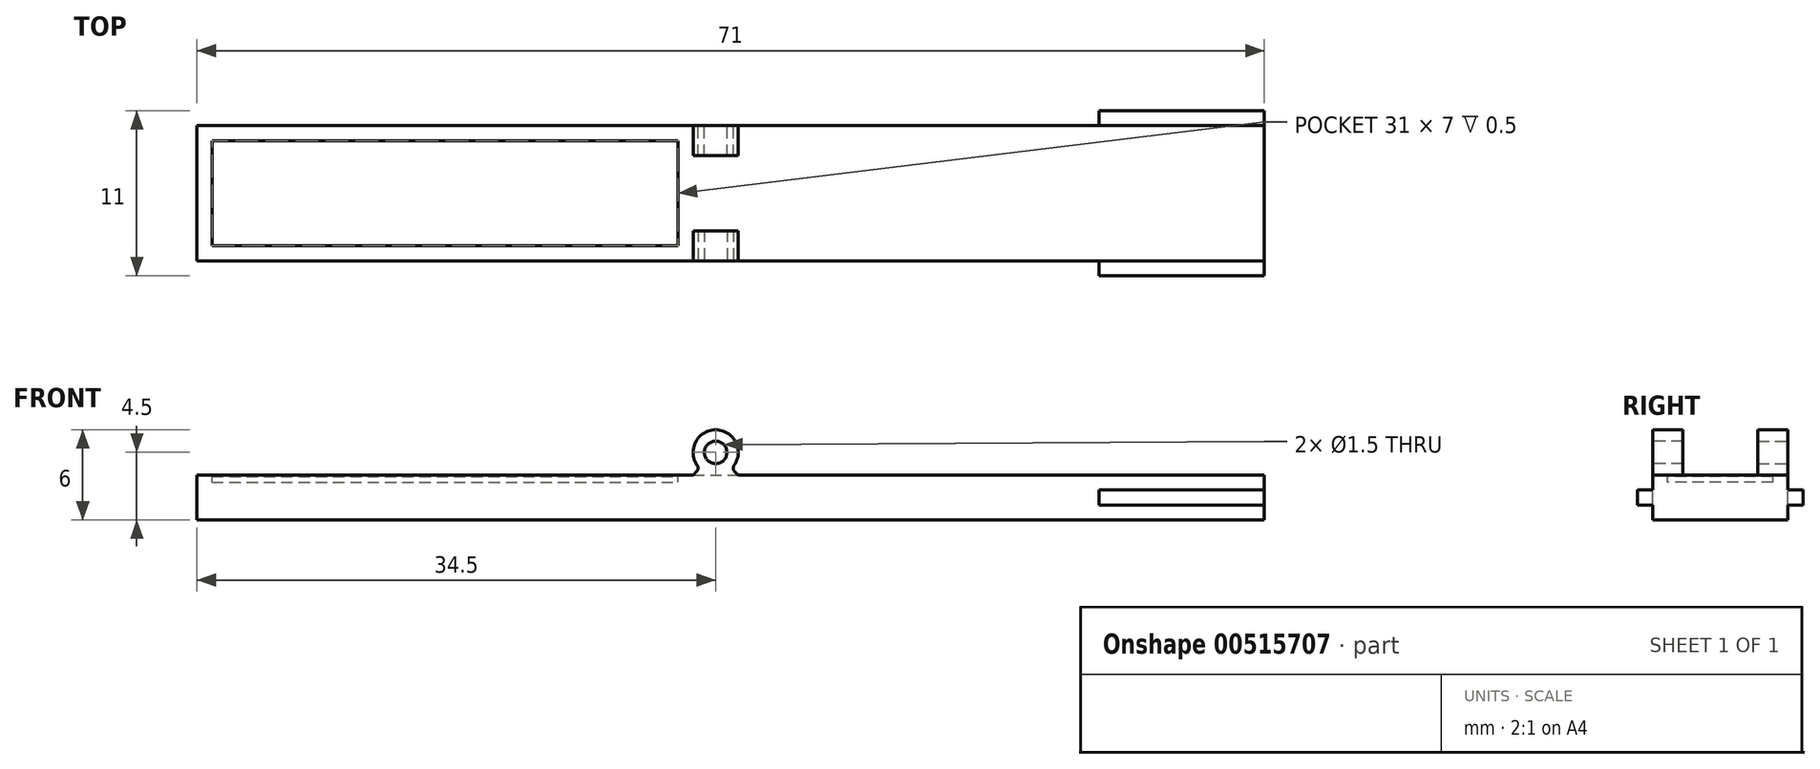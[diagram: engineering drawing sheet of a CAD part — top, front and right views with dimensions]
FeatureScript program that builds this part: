
annotation { "Feature Type Name" : "Feature", "Feature Type Description" : "" }
export const myFeature = defineFeature(function(context is Context, id is Id, definition is map)
    precondition{}
    {
        {
            var Q0;
            Q0=qCreatedBy(makeId("Top.planeOp"),FACE);
            var sketch = newSketch(context, id + "F0", { "sketchPlane" : qUnion([Q0])});
            skLineSegment(sketch, "E0.bottom", {"start": v(-34.5, 4.5) * mm, "end": v(36.5, 4.5) * mm});
            skLineSegment(sketch, "E0.top", {"start": v(-34.5, -4.5) * mm, "end": v(36.5, -4.5) * mm});
            skLineSegment(sketch, "E0.left", {"start": v(-34.5, 4.5) * mm, "end": v(-34.5, -4.5) * mm});
            skLineSegment(sketch, "E0.right", {"start": v(36.5, 4.5) * mm, "end": v(36.5, -4.5) * mm});
            skLineSegment(sketch, "E1", {"start": v(-34.5, 0) * mm, "end": v(36.5, 0) * mm, "construction": true});
            skPoint(sketch, "E1.startSnap0", {"position": v(-34.5, 0) * mm});
            skLineSegment(sketch, "E2", {"start": v(0, 4.5) * mm, "end": v(0, -4.5) * mm, "construction": true});
            skLineSegment(sketch, "E3.bottom", {"start": v(-33.5, 3.5) * mm, "end": v(-2.5, 3.5) * mm});
            skLineSegment(sketch, "E3.top", {"start": v(-33.5, -3.5) * mm, "end": v(-2.5, -3.5) * mm});
            skLineSegment(sketch, "E3.left", {"start": v(-33.5, 3.5) * mm, "end": v(-33.5, -3.5) * mm});
            skLineSegment(sketch, "E3.right", {"start": v(-2.5, 3.5) * mm, "end": v(-2.5, -3.5) * mm});
            skSolve(sketch);
        }
        {
            var Q0;
            Q0=makeQuery(id+"F0.imprint","IMPRINT",FACE,{"disambiguationData":[TD([[makeQuery(id+"F0.imprint","IMPRINT",EDGE,{"derivedFrom":sQuery(id+"F0.wireOp",EDGE,"E0.bottom")}),-1.0]])]});
            var Q1;
            Q1=makeQuery(id+"F0.imprint","IMPRINT",FACE,{"disambiguationData":[TD([[makeQuery(id+"F0.imprint","IMPRINT",EDGE,{"derivedFrom":sQuery(id+"F0.wireOp",EDGE,"E3.bottom")}),-1.0]])]});
            extrude(context, id + "F1", {"entities" : qUnion([Q0, Q1]), "oppositeDirection" : true, "depth" : 3 * mm, "offsetDistance" : 25 * mm});
        }
        {
            var Q0;
            Q0=qCreatedBy(makeId("Front.planeOp"),FACE);
            cPlane(context, id + "F2", {"entities" : qUnion([Q0]), "cplaneType" : CPlaneType.OFFSET, "offset" : 4.5 * mm, "width" : 150 * mm, "height" : 150 * mm});
        }
        {
            var Q0;
            Q0=qCreatedBy(id+"F2.planeOp",FACE);
            var sketch = newSketch(context, id + "F3", { "sketchPlane" : qUnion([Q0])});
            skCircle(sketch, "E4", {"center": v(0, 1.5) * mm, "radius": 1.5 * mm});
            skCircle(sketch, "E5", {"center": v(0, 1.5) * mm, "radius": 0.75 * mm});
            skLineSegment(sketch, "E6", {"start": v(0, -1.6) * mm, "end": v(0, 3.6) * mm, "construction": true});
            skLineSegment(sketch, "E7", {"start": v(1.06, 0.44) * mm, "end": v(1.5, 0) * mm});
            skLineSegment(sketch, "E8", {"start": v(0, 1.5) * mm, "end": v(1.06, 0.44) * mm, "construction": true});
            skLineSegment(sketch, "E9.MirrorCS", {"start": v(-1.06, 0.44) * mm, "end": v(-1.5, 0) * mm});
            skLineSegment(sketch, "E10.0", {"start": v(-1.5, 0) * mm, "end": v(1.5, 0) * mm});
            skPoint(sketch, "E11.orphan", {"position": v(-34.5, 0) * mm});
            skPoint(sketch, "E12.orphan", {"position": v(36.5, 0) * mm});
            skLineSegment(sketch, "E13.right", {"start": v(36.5, -1) * mm, "end": v(36.5, -2) * mm});
            skLineSegment(sketch, "E14.bottom", {"start": v(25.5, -1) * mm, "end": v(35.5, -1) * mm});
            skLineSegment(sketch, "E14.top", {"start": v(25.5, -2) * mm, "end": v(35.5, -2) * mm});
            skLineSegment(sketch, "E14.left", {"start": v(25.5, -1) * mm, "end": v(25.5, -2) * mm});
            skLineSegment(sketch, "E15", {"start": v(18.91, -1.5) * mm, "end": v(36.5, -1.5) * mm, "construction": true});
            skPoint(sketch, "E15.startSnap0", {"position": v(25.5, -1.5) * mm});
            skLineSegment(sketch, "E16", {"start": v(35.5, -2) * mm, "end": v(36.5, -2) * mm});
            skLineSegment(sketch, "E17", {"start": v(35.5, -1) * mm, "end": v(36.5, -1) * mm});
            skPoint(sketch, "E13.top.end.orphan", {"position": v(36.5, -3) * mm});
            skLineSegment(sketch, "E18.0", {"start": v(36.5, -3) * mm, "end": v(36.5, 0) * mm});
            skSolve(sketch);
        }
        {
            var Q0;
            Q0=makeQuery(id+"F3.imprint","IMPRINT",FACE,{"disambiguationData":[TD([[makeQuery(id+"F3.imprint","IMPRINT",EDGE,{"derivedFrom":sQuery(id+"F3.wireOp",EDGE,"E4")}),1.0]])]});
            var Q1;
            {var subQ0=sQuery(id+"F3.wireOp",EDGE,"E9.MirrorCS");Q1=makeQuery(id+"F3.imprint","IMPRINT",FACE,{"disambiguationData":[TD([[makeQuery(id+"F3.imprint","IMPRINT",EDGE,{"derivedFrom":subQ0}),1.0]])]});}
            var Q2;
            {var subQ0=sQuery(id+"F3.wireOp",EDGE,"E7");Q2=makeQuery(id+"F3.imprint","IMPRINT",FACE,{"disambiguationData":[TD([[makeQuery(id+"F3.imprint","IMPRINT",EDGE,{"derivedFrom":subQ0}),-1.0]])]});}
            extrude(context, id + "F4", {"entities" : qUnion([Q0, Q1, Q2]), "operationType" : NewBodyOperationType.ADD, "oppositeDirection" : true, "depth" : 2 * mm, "offsetDistance" : 25 * mm});
        }
        {
            var Q0;
            Q0=makeQuery(id+"F4.opExtrude","SWEPT_EDGE",EDGE,{"disambiguationData":[OSD([sQuery(id+"F3.wireOp",EDGE,"E4"),sQuery(id+"F3.wireOp",EDGE,"E7")])]});
            var Q1;
            Q1=makeQuery(id+"F4.opExtrude","SWEPT_EDGE",EDGE,{"disambiguationData":[OSD([sQuery(id+"F3.wireOp",EDGE,"E4"),sQuery(id+"F3.wireOp",EDGE,"E9.MirrorCS")])]});
            var Q2;
            Q2=makeQuery(id+"F4.opExtrude","SWEPT_EDGE",EDGE,{"disambiguationData":[OSD([sQuery(id+"F3.wireOp",EDGE,"E9.MirrorCS"),sQuery(id+"F3.wireOp",EDGE,"E10.0")])]});
            var Q3;
            Q3=makeQuery(id+"F4.opExtrude","SWEPT_EDGE",EDGE,{"disambiguationData":[OSD([sQuery(id+"F3.wireOp",EDGE,"E7"),sQuery(id+"F3.wireOp",EDGE,"E10.0")])]});
            fillet(context, id + "F5", {"entities" : qUnion([Q0, Q1, Q2, Q3]), "radius" : .3 * mm, "tangentPropagation" : true, "allowEdgeOverflow" : false});
        }
        {
            var Q0;
            Q0=makeQuery(id+"F1.opExtrude","SWEPT_BODY",BODY,{"disambiguationData":[OSD([sQuery(id+"F0.wireOp",EDGE,"E0.bottom"),sQuery(id+"F0.wireOp",EDGE,"E0.top"),sQuery(id+"F0.wireOp",EDGE,"E0.left"),sQuery(id+"F0.wireOp",EDGE,"E0.right")])]});
            var Q1;
            Q1=qCreatedBy(makeId("Front.planeOp"),FACE);
            mirror(context, id + "F6", {"operationType" : NewBodyOperationType.ADD, "entities" : qUnion([Q0]), "mirrorPlane" : qUnion([Q1])});
        }
        {
            var Q0;
            Q0=makeQuery(id+"F3.imprint","IMPRINT",FACE,{"disambiguationData":[TD([[makeQuery(id+"F3.imprint","IMPRINT",EDGE,{"derivedFrom":sQuery(id+"F3.wireOp",EDGE,"E14.bottom")}),-1.0]])]});
            extrude(context, id + "F7", {"entities" : qUnion([Q0]), "operationType" : NewBodyOperationType.ADD, "depth" : 1 * mm, "offsetDistance" : 25 * mm, "hasSecondDirection" : true, "secondDirectionOppositeDirection" : true, "secondDirectionDepth" : 10 * mm});
        }
        {
            var Q0;
            Q0=makeQuery(id+"F0.imprint","IMPRINT",FACE,{"disambiguationData":[TD([[makeQuery(id+"F0.imprint","IMPRINT",EDGE,{"derivedFrom":sQuery(id+"F0.wireOp",EDGE,"E3.bottom")}),-1.0]])]});
            extrude(context, id + "F8", {"entities" : qUnion([Q0]), "operationType" : NewBodyOperationType.REMOVE, "oppositeDirection" : true, "depth" : .5 * mm, "offsetDistance" : 25 * mm});
        }
        {
            var Q0;
            Q0=makeQuery(id+"F0.imprint","IMPRINT",FACE,{"disambiguationData":[TD([[makeQuery(id+"F0.imprint","IMPRINT",EDGE,{"derivedFrom":sQuery(id+"F0.wireOp",EDGE,"E3.bottom")}),-1.0]])]});
            extrude(context, id + "F9", {"entities" : qUnion([Q0]), "oppositeDirection" : true, "depth" : .5 * mm, "offsetDistance" : 25 * mm});
        }
        {
            var Q0;
            Q0=makeQuery(id+"F0.imprint","IMPRINT",FACE,{"disambiguationData":[TD([[makeQuery(id+"F0.imprint","IMPRINT",EDGE,{"derivedFrom":sQuery(id+"F0.wireOp",EDGE,"E3.bottom")}),-1.0]])]});
            extrude(context, id + "F10", {"entities" : qUnion([Q0]), "operationType" : NewBodyOperationType.REMOVE, "oppositeDirection" : true, "depth" : .1 * mm, "offsetDistance" : 25 * mm});
        }
    });
